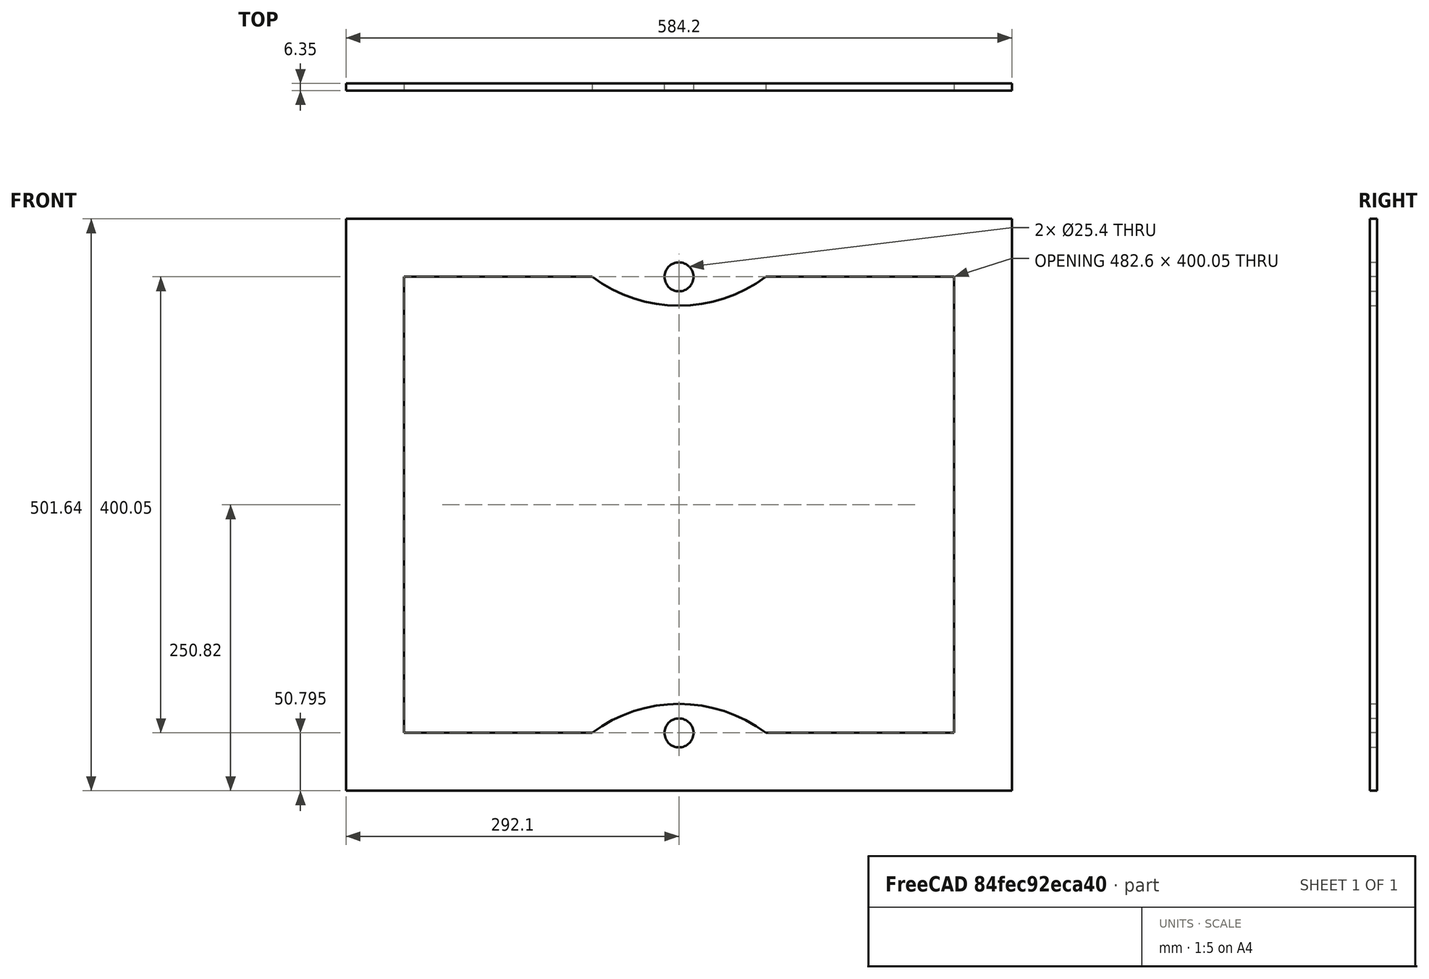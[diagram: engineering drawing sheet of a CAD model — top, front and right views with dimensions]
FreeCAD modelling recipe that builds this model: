
FCSTD DOCUMENT  (FreeCAD 0.16R6712 (Git))
Label: top
License: All rights reserved
LicenseURL: http://en.wikipedia.org/wiki/All_rights_reserved
objects: Sketcher::SketchObject×1, PartDesign::Pad×1
note: 3 computed .brp shape members not serialized (recipe doc carries the construction recipe); baked Part::Feature solids carry a one-line shape summary decoded from their .brp

FEATURE [Sketcher::SketchObject] Sketch002  label="top pattern"
  Placement = pos=(0,304.8,914.4) rot=(1,0,0;1.5708rad)
  sketch-geometry (18):
    g0: LineSegment StartX=-292.1 StartY=250.825 StartZ=0 EndX=292.1 EndY=250.825 EndZ=0
    g1: LineSegment StartX=292.1 StartY=250.825 StartZ=0 EndX=292.1 EndY=-250.825 EndZ=0
    g2: LineSegment StartX=292.1 StartY=-250.825 StartZ=0 EndX=-292.1 EndY=-250.825 EndZ=0
    g3: LineSegment StartX=-292.1 StartY=-250.825 StartZ=0 EndX=-292.1 EndY=250.825 EndZ=0
    g4: LineSegment StartX=-241.3 StartY=200.025 StartZ=0 EndX=-241.3 EndY=-200.025 EndZ=0
    g5: LineSegment StartX=241.3 StartY=200.025 StartZ=0 EndX=241.3 EndY=-200.025 EndZ=0
    g6: LineSegment StartX=-241.3 StartY=200.025 StartZ=0 EndX=-76.2 EndY=200.025 EndZ=0
    g7: LineSegment StartX=241.3 StartY=200.025 StartZ=0 EndX=76.2 EndY=200.025 EndZ=0
    g8: LineSegment StartX=241.3 StartY=-200.025 StartZ=0 EndX=76.2 EndY=-200.025 EndZ=0
    g9: LineSegment StartX=-241.3 StartY=-200.025 StartZ=0 EndX=-76.2 EndY=-200.025 EndZ=0
    g10: LineSegment [constr] StartX=-76.2 StartY=200.025 StartZ=0 EndX=76.2 EndY=200.025 EndZ=0
    g11: LineSegment [constr] StartX=-76.2 StartY=-200.025 StartZ=0 EndX=76.2 EndY=-200.025 EndZ=0
    g12: LineSegment [constr] StartX=241.3 StartY=200.025 StartZ=0 EndX=241.3 EndY=250.825 EndZ=0
    g13: ArcOfCircle CenterX=0 CenterY=-301.625 CenterZ=0 NormalX=0 NormalY=0 NormalZ=1 Radius=127 StartAngle=0.927295 EndAngle=2.2143
    g14: ArcOfCircle CenterX=0 CenterY=301.625 CenterZ=0 NormalX=0 NormalY=0 NormalZ=1 Radius=127 StartAngle=4.06889 EndAngle=5.35589
    g15: Circle CenterX=0 CenterY=200.025 CenterZ=0 NormalX=0 NormalY=0 NormalZ=1 Radius=12.7
    g16: Circle CenterX=0 CenterY=-200.025 CenterZ=0 NormalX=0 NormalY=0 NormalZ=1 Radius=12.7
    g17: LineSegment [constr] StartX=241.3 StartY=200.025 StartZ=0 EndX=292.1 EndY=200.025 EndZ=0
  constraints (54):
    c: Coincident(g0,g1)
    c: Coincident(g1,g2)
    c: Coincident(g2,g3)
    c: Coincident(g3,g0)
    c: Horizontal(g0)
    c: Vertical(g1)
    c: Equal(g1,g3)  'Constraint7'
    c: Equal(g0,g2)
    c: DistanceY(g3,g3) = 501.65
    c: DistanceX(g0,g0) = 584.2
    c: Symmetric(g0,g1,g-1)
    c: Vertical(g5)
    c: Equal(g4,g5)
    c: Coincident(g6,g4)
    c: Horizontal(g6)
    c: Coincident(g7,g5)
    c: Horizontal(g7)
    c: Coincident(g8,g5)
    c: Horizontal(g8)
    c: Coincident(g9,g4)
    c: Horizontal(g9)
    c: Equal(g6,g7)
    c: Equal(g7,g8)
    c: Equal(g8,g9)
    c: Coincident(g10,g6)
    c: Horizontal(g10)
    c: Coincident(g10,g7)
    c: Coincident(g11,g9)
    c: Coincident(g11,g8)
    c: Equal(g11,g10)
    c: Coincident(g12,g5)
    c: PointOnObject(g12,g0)
    c: Vertical(g12)
    c: DistanceY(g12,g12) = 50.8
    c: Symmetric(g4,g4,g-1)
    c: DistanceX(g11,g11) = 152.4
    c: Coincident(g13,g9)
    c: Coincident(g13,g8)
    c: Radius(g13) = 127
    c: Coincident(g14,g6)
    c: Coincident(g14,g7)
    c: Equal(g14,g13)
    c: PointOnObject(g15,g10)
    c: Symmetric(g6,g7,g15)
    c: Radius(g15) = 12.7
    c: PointOnObject(g16,g11)
    c: Equal(g16,g15)
    c: Symmetric(g9,g8,g16)
    c: Symmetric(g2,g0,g-1)
    c: Coincident(g17,g5)
    c: PointOnObject(g17,g1)
    c: Horizontal(g17)
    c: Equal(g17,g12)
    c: Symmetric(g4,g5,g-1)
FEATURE [PartDesign::Pad] Pad008  label="top"
  Length = 6.35
  Length2 = 100
  Placement = pos=(0,304.8,914.4) rot=(1,0,0;1.5708rad)
  Sketch = -> Sketch002
  Type = 0
